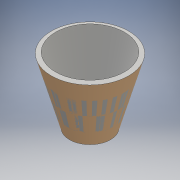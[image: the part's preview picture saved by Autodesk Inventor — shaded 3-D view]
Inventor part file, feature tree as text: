
AUTODESK INVENTOR PART (.ipt)
format: ipt  version: 2016 (Build 200138000, 138)  size: 118,272 bytes
history: native  units: mm
features: sketch x2, plane x1, thicken_offset x1, other x1, loft x1
ambient origin geometry x8: Origin, YZ Plane, XZ Plane, XY Plane, X Axis, Y Axis, Z Axis, Center Point
bodies: Body1 (feature_tree), Body2 (feature_tree)
feature tree (6):
  sketch  "Sketch1"  dims[d0=168.0mm d1=9.52mm]
  plane  "Work Plane1"
  thicken_offset  "Thicken1"
  sketch  "Sketch2"  dims[d2=-140.0mm d3=89.0mm d4=9.52mm d15=0.0mm d16=90.0deg d17=0.0mm d18=90.0deg d19=9.52mm d20=9.52mm]
  other  "Srf1"
  loft  "LoftSrf1"
